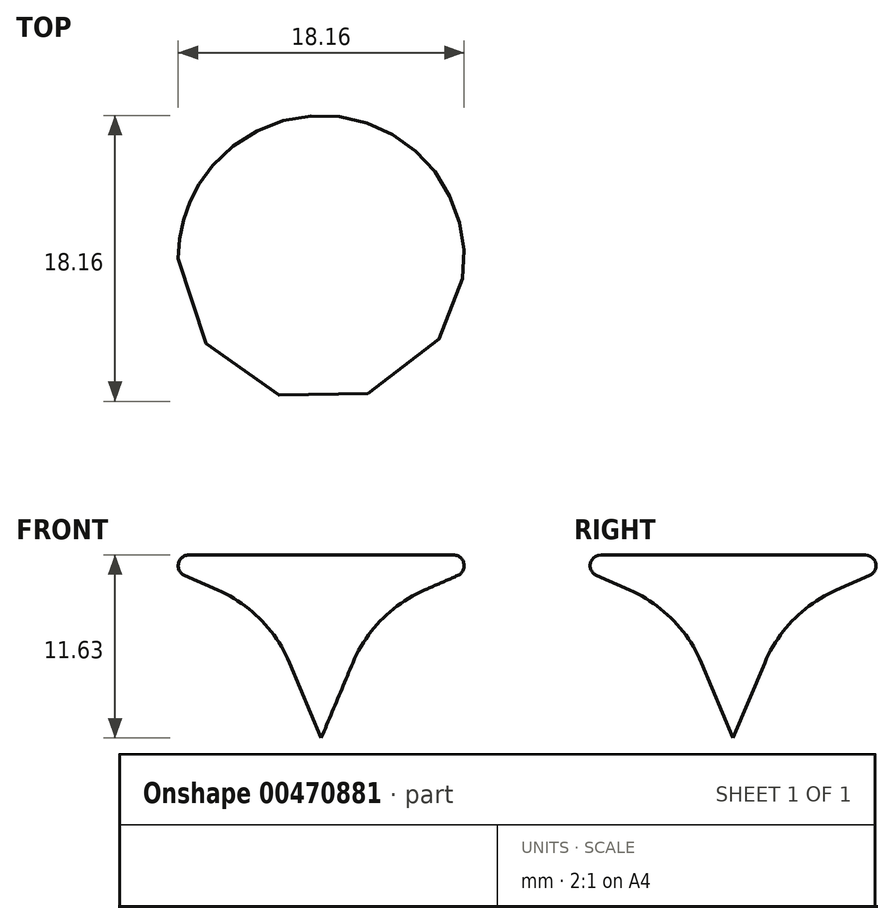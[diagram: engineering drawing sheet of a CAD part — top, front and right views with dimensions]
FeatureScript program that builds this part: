
annotation { "Feature Type Name" : "Feature", "Feature Type Description" : "" }
export const myFeature = defineFeature(function(context is Context, id is Id, definition is map)
    precondition{}
    {
        {
            var Q0;
            Q0=qCreatedBy(makeId("Front.planeOp"),FACE);
            var sketch = newSketch(context, id + "F0", { "sketchPlane" : qUnion([Q0])});
            skLineSegment(sketch, "E0", {"start": v(0, 0) * mm, "end": v(3.37, 8) * mm});
            skLineSegment(sketch, "E1", {"start": v(3.37, 8) * mm, "end": v(11.66, 11.63) * mm});
            skLineSegment(sketch, "E2", {"start": v(11.66, 11.63) * mm, "end": v(0, 11.63) * mm});
            skLineSegment(sketch, "E3", {"start": v(0, 11.63) * mm, "end": v(0, 0) * mm});
            skSolve(sketch);
        }
        {
            var Q0;
            Q0 = qSketchRegion(id + "F0", true);
            var Q1;
            Q1=sQuery(id+"F0.wireOp",EDGE,"E3");
            revolve(context, id + "F1", {"entities" : qUnion([Q0]), "axis" : qUnion([Q1]), "revolveType" : RevolveType.FULL});
        }
        {
            var Q0;
            Q0=makeQuery(id+"F1.opRevolve","SWEPT_EDGE",EDGE,{"disambiguationData":[OSD([sQuery(id+"F0.wireOp",EDGE,"E1"),sQuery(id+"F0.wireOp",EDGE,"E2")])]});
            fillet(context, id + "F2", {"entities" : qUnion([Q0]), "radius" : 0.68 * mm, "tangentPropagation" : true, "allowEdgeOverflow" : false});
        }
        {
            var Q0;
            Q0=makeQuery(id+"F1.opRevolve","SWEPT_EDGE",EDGE,{"disambiguationData":[OSD([sQuery(id+"F0.wireOp",EDGE,"E0"),sQuery(id+"F0.wireOp",EDGE,"E1")])]});
            fillet(context, id + "F3", {"entities" : qUnion([Q0]), "radius" : 8.75 * mm, "tangentPropagation" : true, "allowEdgeOverflow" : false});
        }
    });
